# Revit family: IS_Retta_B8988_BIM_DE
name_source: partatom
category: Plumbing Fixtures
revit_build: Autodesk Revit MEP 2016 (Build: 20161004_0715(x64)
units: mm (PartAtom-declared; Revit-internal decimal feet)

## family parameters
Always vertical = No
Cut with Voids When Loaded = No
OmniClass Number = 23.45.55.17
OmniClass Title = Mixing Faucets
Part Type = Normal
Room Calculation Point = No
Round Connector Dimension = Use Diameter
Shared = No
Work Plane-Based = No

## types (1)
- B8988AA - RETTA kitchen mixer one hole single lever hand with pull out spout, low pressure
    Accessories = www.idealstandard.de\ersatzteile
    AssetType = Fixed
    BIMObjectName = ISI_IdealStandard_SinkManualWaterSupplySets_Retta_B8988AA
    BIMobject category = Taps & Mixers
    BOSUseNativeGeometries = 1
    BarCode = 3800861016892
    Brand = Ideal Standard
    Brand url = http://www.idealstandard.de
    CodePerformance = 0
    Color = Chrome
    ConnectionType = Plumbing
    Cost = 0 $
    CurrencyUnit = €
    CurrentRevision = 1
    Date of publishing = 20/12/2017
    Description = IS Küchenarmatur RETTA ND mit herausziehbarer Handbrause Chrom
    DurationUnit = Year
    EAN code = https://3800861016892
    Edition number = 1
    ExpectedLife = 25
    Features = IS Küchenarmatur RETTA ND mit herausziehbarer Handbrause Chrom
    Finish = Chrome
    IFC Classification = Sanitary Terminal
    IfcExportAs = IfcSanitaryTerminalType
    InletConnectionSize = 0 mm  [stored 0 ft]
    Installation instructions = http://www.idealstandard.de
    InstallationInstructions = www.idealstandard.de\produkte
    MainColor = Chrome
    MaintenanceInformation = www.idealstandard.de\produkte
    Manufacturer name = Ideal Standard
    ManufacturerURL = http://www.idealstandard.de
    Material = Brass
    Material main = Brass
    Model = B8988AA
    ModelNumber = B8988AA
    ModelReference = IS Küchenarmatur RETTA ND mit herausziehbarer Handbrause Chrom
    NBS Reference Code = 35-79-79
    NBS Reference Description = Sink Water Supply Fittings
    Name = SinkManualWaterSupplySets_Retta_B8988AA
    NettWeight = 3.02 Kg
    Nominal height = 0
    Nominal width = 0
    NominalDepth = 269 mm
    NominalHeight = 243 mm
    NominalLength = 269 mm
    NominalWidth = 56 mm
    OmniClass Code = 23-31 11 00
    OmniClass Description = Faucets
    Product Guid = cef07291-73a2-485a-9461-cb73b2f2cd33
    Product SKU = B8988
    Product data url = https://bimobject.com
    Product family = Sanitary
    Product group = Kitchen Mixer
    Product name = RETTA kitchen mixer one hole single lever hand with pull out spout, low pressure
    Product url = http://www.idealstandard.de
    ProductInformation = www.idealstandard.de/produkte
    QR code = http://bimobject.com
    Shape = Sculptured
    Size = 243 x 270 x 56mm
    Space = Internal
    SpareParts = www.idealstandard.de/ersatzteile
    Technical description = http://www.idealstandard.de
    TestPressure = 10 Bar
    URL = http://www.idealstandard.de
    Uniclass 1.4 Code = L8212
    Uniclass 1.4 Description = Fittings
    Uniclass 2.0 Code = PR-35-79-79
    Uniclass 2.0 Description = Sink Water Supply Fittings
    Uniclass 2015 Code = Pr_40_20_87_82
    Uniclass 2015 Name = Sink manual water supply sets
    Uniclass2015Code = Pr_40_20_87_82
    Uniclass2015Title = Sink manual water supply sets
    Uniclass2015Version = Products v1.1
    Version = 1
    VolumeUnits = Litres
    Weight Net (Kg) = 3.02

note: [stored X ft] marks values corroborated as IEEE doubles in the binary element streams (Revit-internal decimal feet)

## geometry (parser evidence)
native form markers: Blend x2, Sweep x3
no freeform markers — native parametric forms only
